# Revit family: 07711_DAO-H_1R
name_source: partatom
category: Air Terminals
revit_build: Autodesk Revit MEP 2012 (Build: 20110309_2315(x64)
units: mm (PartAtom-declared; Revit-internal decimal feet)

## types (5) — shared parameters
Description = Difusor Lineal Oculto
Función = Inyección
Longitud Mín-Máx. = 24" (0.6096 mts)  a 141 3/4" (3.60 mts)
Manufacturer = INNES
Material del Difusor = Aluminio y acero
Model = DAO-H-1R
Nota1 = .
Nota2 = .
Posición de Instalación = Muro/Techo
Tipo de Cuello = Rectangular
Type Comments = Descarga Horizontal con 1 Ranura
URL = https://www.innes.com.mx
Visible_Texto_1 = No
Visible_Texto_2 = No

## per-type parameters (varying)
| type | Conect_Ancho | Conect_Largo | Largo_Requerido | Separacion | Var1 |
| Separación 1" | 2 171/256" | 72" | 72" | 1" | 36" |
| Separación 1.5" | 3 37/256" | 72" | 72" | 1 1/2" | 36" |
| Separación 2" | 3 171/256" | 36" | 36" | 2" | 18" |
| Separación 2.5" | 4 37/256" | 36" | 36" | 2 1/2" | 18" |
| Separación 3" | 4 171/256" | 36" | 36" | 3" | 18" |

## geometry (parser evidence)
native form markers: Sweep x11
no freeform markers — native parametric forms only
